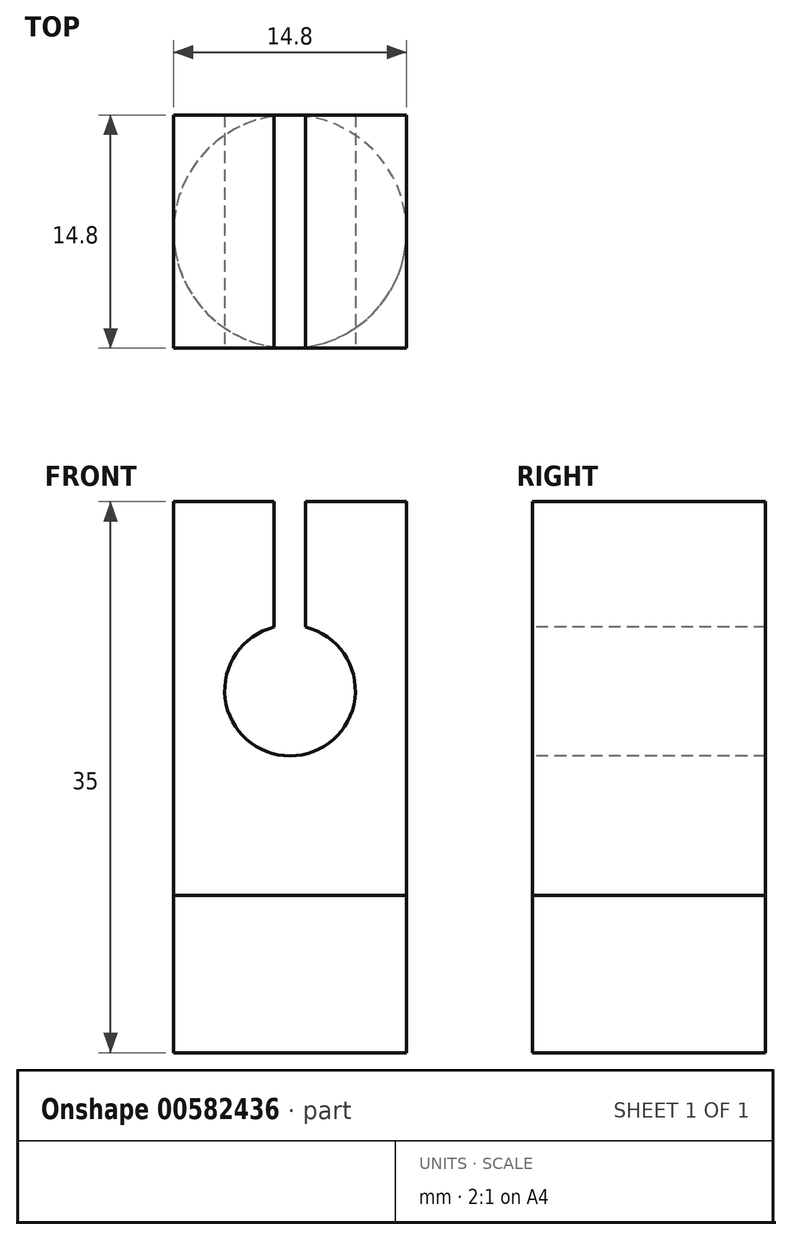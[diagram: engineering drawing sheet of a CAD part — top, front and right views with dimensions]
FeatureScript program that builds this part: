
annotation { "Feature Type Name" : "Feature", "Feature Type Description" : "" }
export const myFeature = defineFeature(function(context is Context, id is Id, definition is map)
    precondition{}
    {
        {
            var Q0;
            Q0=qCreatedBy(makeId("Top.planeOp"),FACE);
            var sketch = newSketch(context, id + "F0", { "sketchPlane" : qUnion([Q0])});
            skCircle(sketch, "E0", {"center": v(0, 0) * mm, "radius": 7.4 * mm});
            skSolve(sketch);
        }
        {
            var Q0;
            Q0 = qSketchRegion(id + "F0", true);
            extrude(context, id + "F1", {"entities" : qUnion([Q0]), "oppositeDirection" : true, "depth" : 10 * mm, "offsetDistance" : 25 * mm});
        }
        {
            var Q0;
            Q0=makeQuery(id+"F1.opExtrude","CAP_FACE",FACE,{"disambiguationData":[OSD([sQuery(id+"F0.wireOp",EDGE,"E0")])],"isStart":true});
            var sketch = newSketch(context, id + "F2", { "sketchPlane" : qUnion([Q0])});
            skLineSegment(sketch, "E1.bottom", {"start": v(7.4, 7.4) * mm, "end": v(-7.4, 7.4) * mm});
            skLineSegment(sketch, "E1.top", {"start": v(7.4, -7.4) * mm, "end": v(-7.4, -7.4) * mm});
            skLineSegment(sketch, "E1.left", {"start": v(7.4, 7.4) * mm, "end": v(7.4, -7.4) * mm});
            skLineSegment(sketch, "E1.right", {"start": v(-7.4, 7.4) * mm, "end": v(-7.4, -7.4) * mm});
            skPoint(sketch, "E1.middle", {"position": v(0, 0) * mm});
            skSolve(sketch);
        }
        {
            var Q0;
            Q0 = qSketchRegion(id + "F2", true);
            extrude(context, id + "F3", {"entities" : qUnion([Q0]), "operationType" : NewBodyOperationType.ADD, "depth" : 25 * mm, "offsetDistance" : 25 * mm});
        }
        {
            var Q0;
            Q0=qCreatedBy(makeId("Front.planeOp"),FACE);
            var sketch = newSketch(context, id + "F4", { "sketchPlane" : qUnion([Q0])});
            skCircle(sketch, "E2", {"center": v(0, 13) * mm, "radius": 4.15 * mm});
            skLineSegment(sketch, "E3.bottom", {"start": v(-1, 25) * mm, "end": v(1, 25) * mm});
            skLineSegment(sketch, "E3.top", {"start": v(-1, 13) * mm, "end": v(1, 13) * mm});
            skLineSegment(sketch, "E3.left", {"start": v(-1, 25) * mm, "end": v(-1, 13) * mm});
            skLineSegment(sketch, "E3.right", {"start": v(1, 25) * mm, "end": v(1, 13) * mm});
            skSolve(sketch);
        }
        {
            var Q0;
            Q0 = qSketchRegion(id + "F4", true);
            extrude(context, id + "F5", {"entities" : qUnion([Q0]), "operationType" : NewBodyOperationType.REMOVE, "endBound" : BoundingType.SYMMETRIC, "oppositeDirection" : true, "depth" : 25 * mm, "offsetDistance" : 25 * mm});
        }
    });
